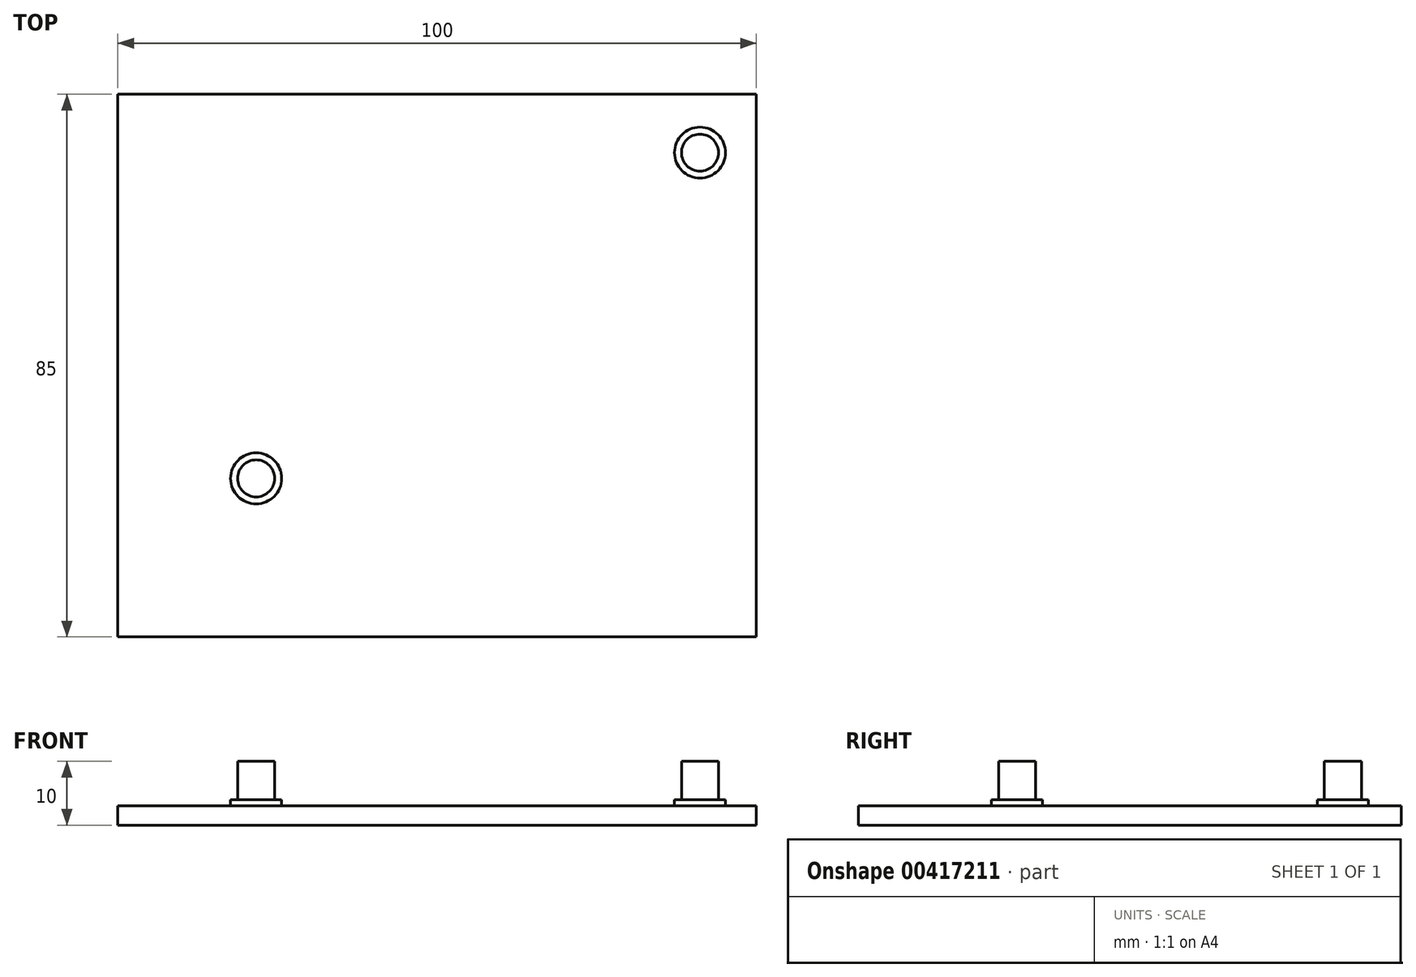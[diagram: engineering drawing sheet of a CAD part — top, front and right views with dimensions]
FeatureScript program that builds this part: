
annotation { "Feature Type Name" : "Feature", "Feature Type Description" : "" }
export const myFeature = defineFeature(function(context is Context, id is Id, definition is map)
    precondition{}
    {
        {
            var Q0;
            Q0=qCreatedBy(makeId("Top.planeOp"),FACE);
            var sketch = newSketch(context, id + "F0", { "sketchPlane" : qUnion([Q0])});
            skLineSegment(sketch, "E0.bottom", {"start": v(-65.35, -36.21) * mm, "end": v(34.65, -36.21) * mm});
            skLineSegment(sketch, "E0.top", {"start": v(-65.35, 48.79) * mm, "end": v(34.65, 48.79) * mm});
            skLineSegment(sketch, "E0.left", {"start": v(-65.35, -36.21) * mm, "end": v(-65.35, 48.79) * mm});
            skLineSegment(sketch, "E0.right", {"start": v(34.65, -36.21) * mm, "end": v(34.65, 48.79) * mm});
            skSolve(sketch);
        }
        {
            var Q0;
            Q0 = qSketchRegion(id + "F0", true);
            extrude(context, id + "F1", {"entities" : qUnion([Q0]), "depth" : 3 * mm});
        }
        {
            var Q0;
            Q0=makeQuery(id+"F1.opExtrude","CAP_FACE",FACE,{"disambiguationData":[OSD([sQuery(id+"F0.wireOp",EDGE,"E0.bottom"),sQuery(id+"F0.wireOp",EDGE,"E0.top"),sQuery(id+"F0.wireOp",EDGE,"E0.left"),sQuery(id+"F0.wireOp",EDGE,"E0.right")])],"isStart":false});
            var sketch = newSketch(context, id + "F2", { "sketchPlane" : qUnion([Q0])});
            skCircle(sketch, "E1", {"center": v(-43.7, -11.39) * mm, "radius": 2.9 * mm});
            skCircle(sketch, "E2", {"center": v(25.82, 39.66) * mm, "radius": 2.9 * mm});
            skCircle(sketch, "E3", {"center": v(-43.7, -11.39) * mm, "radius": 4 * mm});
            skCircle(sketch, "E4", {"center": v(25.82, 39.66) * mm, "radius": 4 * mm});
            skSolve(sketch);
        }
        {
            var Q0;
            Q0=makeQuery(id+"F2.imprint","IMPRINT",FACE,{"disambiguationData":[TD([[makeQuery(id+"F2.imprint","IMPRINT",EDGE,{"derivedFrom":sQuery(id+"F2.wireOp",EDGE,"E1")}),1.0]])]});
            var Q1;
            Q1=makeQuery(id+"F2.imprint","IMPRINT",FACE,{"disambiguationData":[TD([[makeQuery(id+"F2.imprint","IMPRINT",EDGE,{"derivedFrom":sQuery(id+"F2.wireOp",EDGE,"E2")}),1.0]])]});
            extrude(context, id + "F3", {"entities" : qUnion([Q0, Q1]), "operationType" : NewBodyOperationType.ADD, "depth" : 7 * mm});
        }
        {
            var Q0;
            Q0=makeQuery(id+"F2.imprint","IMPRINT",FACE,{"disambiguationData":[TD([[makeQuery(id+"F2.imprint","IMPRINT",EDGE,{"derivedFrom":sQuery(id+"F2.wireOp",EDGE,"E1")}),-1.0]])]});
            var Q1;
            Q1=makeQuery(id+"F2.imprint","IMPRINT",FACE,{"disambiguationData":[TD([[makeQuery(id+"F2.imprint","IMPRINT",EDGE,{"derivedFrom":sQuery(id+"F2.wireOp",EDGE,"E2")}),-1.0]])]});
            extrude(context, id + "F4", {"entities" : qUnion([Q0, Q1]), "operationType" : NewBodyOperationType.ADD, "depth" : 1 * mm});
        }
    });
